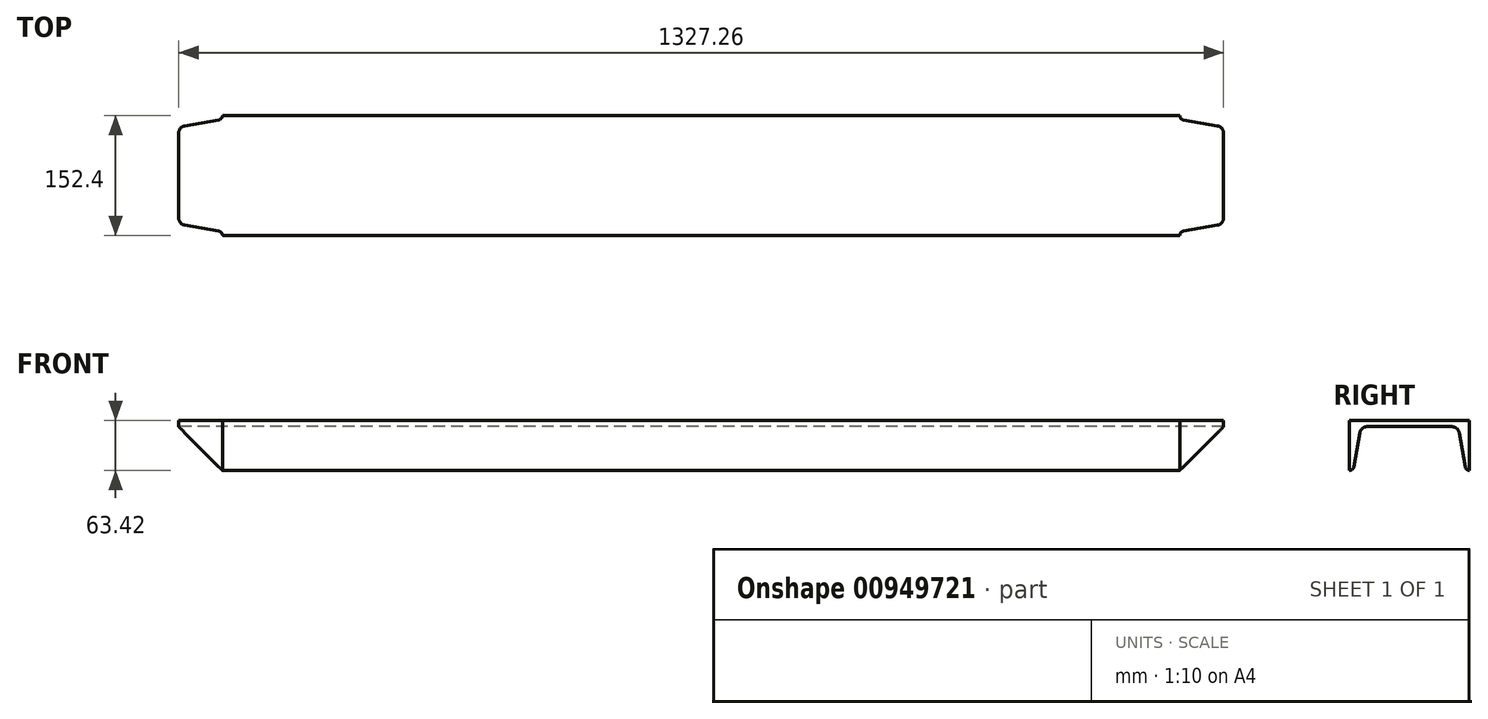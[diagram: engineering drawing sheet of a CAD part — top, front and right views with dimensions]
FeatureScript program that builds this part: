
annotation { "Feature Type Name" : "Feature", "Feature Type Description" : "" }
export const myFeature = defineFeature(function(context is Context, id is Id, definition is map)
    precondition{}
    {
        {
            var Q0;
            Q0=qCreatedBy(makeId("Right.planeOp"),FACE);
            var sketch = newSketch(context, id + "F0", { "sketchPlane" : qUnion([Q0])});
            skLineSegment(sketch, "E0", {"start": v(-76.2, 0) * mm, "end": v(76.2, 0) * mm});
            skLineSegment(sketch, "E1", {"start": v(76.2, 0) * mm, "end": v(76.2, -63.42) * mm});
            skLineSegment(sketch, "E2", {"start": v(-76.2, 0) * mm, "end": v(-76.2, -63.42) * mm});
            skLineSegment(sketch, "E3", {"start": v(-63.12, -15.57) * mm, "end": v(-70.65, -58.76) * mm});
            skLineSegment(sketch, "E4", {"start": v(63.12, -15.57) * mm, "end": v(70.65, -58.76) * mm});
            skLineSegment(sketch, "E5", {"start": v(-53.98, -7.87) * mm, "end": v(53.98, -7.87) * mm});
            skArc(sketch, "E6.filletArc", {"start": v(-76.2, -63.42) * mm, "mid": v(-72.57, -62.1) * mm, "end": v(-70.65, -58.76) * mm});
            skArc(sketch, "E7.filletArc", {"start": v(70.65, -58.76) * mm, "mid": v(72.57, -62.1) * mm, "end": v(76.2, -63.42) * mm});
            skArc(sketch, "E8.filletArc", {"start": v(-53.98, -7.87) * mm, "mid": v(-59.95, -10.05) * mm, "end": v(-63.12, -15.57) * mm});
            skArc(sketch, "E9.filletArc", {"start": v(63.12, -15.57) * mm, "mid": v(59.95, -10.05) * mm, "end": v(53.98, -7.87) * mm});
            skSolve(sketch);
        }
        {
            var Q0;
            Q0=qSketchRegion(id+"F0",true);
            extrude(context, id + "F1", {"entities" : qUnion([Q0]), "depth" : 1343 * mm, "offsetDistance" : 25.4 * mm});
        }
        {
            var Q0;
            Q0=makeQuery(id+"F1.opExtrude","SWEPT_FACE",FACE,{"disambiguationData":[OSD([sQuery(id+"F0.wireOp",EDGE,"E0")])]});
            var sketch = newSketch(context, id + "F2", { "sketchPlane" : qUnion([Q0])});
            skLineSegment(sketch, "E10", {"start": v(1343, 76.2) * mm, "end": v(1343, -76.2) * mm});
            skLineSegment(sketch, "E11", {"start": v(1343, -76.2) * mm, "end": v(1279.58, -76.2) * mm});
            skLineSegment(sketch, "E12", {"start": v(1343, 76.2) * mm, "end": v(1279.58, 76.2) * mm});
            skLineSegment(sketch, "E13", {"start": v(1327.43, 63.12) * mm, "end": v(1284.24, 70.65) * mm});
            skLineSegment(sketch, "E14", {"start": v(1327.43, -63.12) * mm, "end": v(1284.24, -70.65) * mm});
            skLineSegment(sketch, "E15", {"start": v(1335.13, 53.98) * mm, "end": v(1335.13, -53.98) * mm});
            skArc(sketch, "E16.filletArc", {"start": v(1279.58, 76.2) * mm, "mid": v(1280.9, 72.57) * mm, "end": v(1284.24, 70.65) * mm});
            skArc(sketch, "E17.filletArc", {"start": v(1284.24, -70.65) * mm, "mid": v(1280.9, -72.57) * mm, "end": v(1279.58, -76.2) * mm});
            skArc(sketch, "E18.filletArc", {"start": v(1335.13, 53.98) * mm, "mid": v(1332.95, 59.95) * mm, "end": v(1327.43, 63.12) * mm});
            skArc(sketch, "E19.filletArc", {"start": v(1327.43, -63.12) * mm, "mid": v(1332.95, -59.95) * mm, "end": v(1335.13, -53.98) * mm});
            skLineSegment(sketch, "E20", {"start": v(671.5, 76.2) * mm, "end": v(671.5, -76.2) * mm, "construction": true});
            skArc(sketch, "E21.MirrorCS", {"start": v(7.87, 53.98) * mm, "mid": v(10.05, 59.95) * mm, "end": v(15.57, 63.12) * mm});
            skArc(sketch, "E22.MirrorCS", {"start": v(63.42, 76.2) * mm, "mid": v(62.1, 72.57) * mm, "end": v(58.76, 70.65) * mm});
            skArc(sketch, "E23.MirrorCS", {"start": v(15.57, -63.12) * mm, "mid": v(10.05, -59.95) * mm, "end": v(7.87, -53.98) * mm});
            skArc(sketch, "E24.MirrorCS", {"start": v(58.76, -70.65) * mm, "mid": v(62.1, -72.57) * mm, "end": v(63.42, -76.2) * mm});
            skLineSegment(sketch, "E25.MirrorCS", {"start": v(0, 76.2) * mm, "end": v(63.42, 76.2) * mm});
            skLineSegment(sketch, "E26.MirrorCS", {"start": v(15.57, 63.12) * mm, "end": v(58.76, 70.65) * mm});
            skLineSegment(sketch, "E27.MirrorCS", {"start": v(15.57, -63.12) * mm, "end": v(58.76, -70.65) * mm});
            skLineSegment(sketch, "E28.MirrorCS", {"start": v(7.87, 53.98) * mm, "end": v(7.87, -53.98) * mm});
            skLineSegment(sketch, "E29.MirrorCS", {"start": v(0, 76.2) * mm, "end": v(0, -76.2) * mm});
            skLineSegment(sketch, "E30.MirrorCS", {"start": v(0, -76.2) * mm, "end": v(63.42, -76.2) * mm});
            skSolve(sketch);
        }
        {
            var Q0;
            Q0=qSketchRegion(id+"F2",true);
            extrude(context, id + "F3", {"entities" : qUnion([Q0]), "operationType" : NewBodyOperationType.REMOVE, "endBound" : BoundingType.THROUGH_ALL, "oppositeDirection" : true, "depth" : 25.4 * mm, "offsetDistance" : 25.4 * mm});
        }
    });
